# Revit family: IS_UltraFlat_K5183_BIM_BE
name_source: partatom
category: Plumbing Fixtures
revit_build: Autodesk Revit 2015 (Build: 20140606_1530(x64)
units: mm (PartAtom-declared; Revit-internal decimal feet)

## types (1)
- K518301 - Ultra flat Receveur rectangulaire 1200 mm
    Accesoires = www.idealstandard.be
    Afwerking = Wit
    Auteur = Ideal Standard Produktions-GmbH
    Barcode = 4015413013178
    Barrièrevrijwonen = besluit van de Vlaamse regering van 5 juni 2n/an/a9 tot vaststelling van een gewestelijke stendbouwkundige verordening inzake toegankelijkheid.
Artikel 31.3.c
    Beschrijvingdouchekop = 0
    Beschrijvinggarantie = Fabrieksgarantie
    BimObjectNaam = ISI_IdealStandard_Douche_Ultra_K518301
    Breedte = 0
    BrutoGewicht = 0
    Cost = 0 $
    Default Elevation = 0 mm  [stored 0 ft]
    Description = Ultra flat Receveur rectangulaire 1200 mm
    Diepte = 0 mm  [stored 0 ft]
    Dimensions = 900 x 1200 x 30 mm
    Douchebak = No
    DuurEenheid = jaar
    Eigenschappen = Ultra Flat rechthoekige douchebak 120x90 in acryl. Vervaardigd volgens DIN 14527. Met glasvezel verstevigd en ingewerkte bodem- en randversteviging. afloopgat Ø90 mm. Potenset separaat te bestellen.
Vanaf 120 cm : 2 potensets plaatsen.
    Garantieonderdelen = 10
    GrootteAfvoergat = 0
    Hauteur = 30 mm
    IfcExportAs = IfcSanitaryTerminalType
    IfcExportType = SHOWERS
    Installatieinstructies = www.idealstandard.be
    Kleur = Wit
    Largeur = 1200 mm
    Lengte = 0 mm  [stored 0 ft]
    Longueur = 900 mm
    Manufacturer = www.idealstandard.be
    Materiaal = Acryl
    Merk = Ideal Standard
    Model = K518301
    Nettogewicht = 27
    Normen = DIN 14527
    Productinformatie = www.idealstandard.be
    Telefoonnummer = 0032 2 325 66 00
    Typeconnectie = Sanitair
    URL = www.idealstandard.be
    Uniclass2015Beschrijving = Douche
    Uniclass2015Version = Products v1.1
    Urlproducent = www.idealstandard.be
    Versie = 1
    Vervangingskosten = 0
    Verwachtelevensduur = 25 jaar
    Volumeunits = liter
    Vorm = rechthoekig

note: [stored X ft] marks values corroborated as IEEE doubles in the binary element streams (Revit-internal decimal feet)

## geometry (parser evidence)
native form markers: Blend x4, Sweep x1
no freeform markers — native parametric forms only
